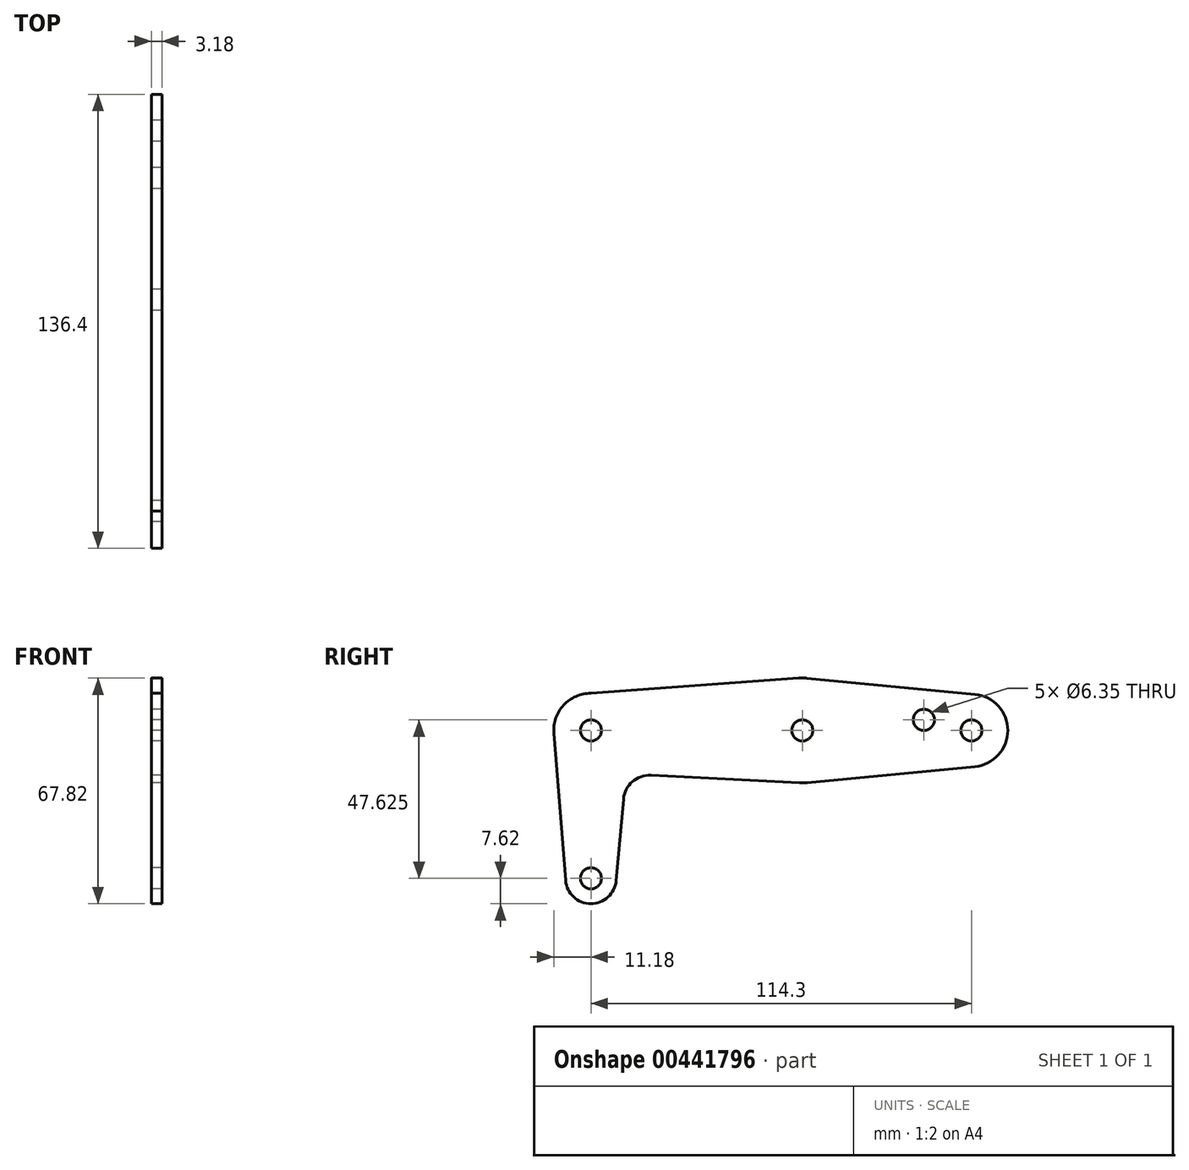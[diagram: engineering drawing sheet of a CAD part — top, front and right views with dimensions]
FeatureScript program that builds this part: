
annotation { "Feature Type Name" : "Feature", "Feature Type Description" : "" }
export const myFeature = defineFeature(function(context is Context, id is Id, definition is map)
    precondition{}
    {
        {
            var Q0;
            Q0=qCreatedBy(makeId("Right.planeOp"),FACE);
            var sketch = newSketch(context, id + "F0", { "sketchPlane" : qUnion([Q0])});
            skArc(sketch, "E0", {"start": v(1.5, 15.68) * mm, "mid": v(0.18, 15.75) * mm, "end": v(-1.13, 15.7) * mm});
            skLineSegment(sketch, "E1", {"start": v(0, 0) * mm, "end": v(-80.01, 0) * mm});
            skLineSegment(sketch, "E2", {"start": v(0, 0) * mm, "end": v(68.5, 0) * mm});
            skLineSegment(sketch, "E3.0", {"start": v(-54.4, -44.45) * mm, "end": v(-72.8, -44.45) * mm});
            skLineSegment(sketch, "E4", {"start": v(0, 22.2) * mm, "end": v(0, -18.9) * mm});
            skLineSegment(sketch, "E5.0", {"start": v(-63.5, 11.2) * mm, "end": v(-63.5, -52.07) * mm});
            skArc(sketch, "E6", {"start": v(-71.1, -45.06) * mm, "mid": v(-63.54, -52.07) * mm, "end": v(-55.91, -45.13) * mm});
            skArc(sketch, "E7", {"start": v(-63.5, 11.18) * mm, "mid": v(-71.71, 7.58) * mm, "end": v(-74.64, -0.9) * mm});
            skLineSegment(sketch, "E8", {"start": v(-74.64, -0.9) * mm, "end": v(-71.1, -45.06) * mm});
            skLineSegment(sketch, "E9.0", {"start": v(-45.87, -21.34) * mm, "end": v(-80.01, -21.34) * mm});
            skLineSegment(sketch, "E10.0", {"start": v(-45.87, 12.48) * mm, "end": v(-45.87, -21.34) * mm});
            skLineSegment(sketch, "E11.0", {"start": v(50.8, 3.18) * mm, "end": v(50.8, -3.18) * mm});
            skArc(sketch, "E12", {"start": v(51.84, -10.87) * mm, "mid": v(61.72, 0) * mm, "end": v(51.84, 10.87) * mm});
            skLineSegment(sketch, "E13", {"start": v(1.5, 15.68) * mm, "end": v(51.84, 10.87) * mm});
            skLineSegment(sketch, "E14", {"start": v(1.5, -15.68) * mm, "end": v(51.84, -10.87) * mm});
            skCircle(sketch, "E15", {"center": v(50.8, 0) * mm, "radius": 3.18 * mm});
            skCircle(sketch, "E16", {"center": v(0, 0) * mm, "radius": 3.18 * mm});
            skLineSegment(sketch, "E17", {"start": v(-1.13, 15.7) * mm, "end": v(-64.3, 11.15) * mm});
            skLineSegment(sketch, "E18", {"start": v(-53.71, -20.63) * mm, "end": v(-55.91, -45.13) * mm});
            skLineSegment(sketch, "E19", {"start": v(-0.8, -15.73) * mm, "end": v(-45.48, -13.47) * mm});
            skArc(sketch, "E20.filletArc", {"start": v(-45.48, -13.47) * mm, "mid": v(-51.04, -15.4) * mm, "end": v(-53.71, -20.63) * mm});
            skArc(sketch, "E21.trimOffspring", {"start": v(-0.8, -15.73) * mm, "mid": v(0.35, -15.74) * mm, "end": v(1.5, -15.68) * mm});
            skCircle(sketch, "E22", {"center": v(-63.5, 0) * mm, "radius": 3.18 * mm});
            skCircle(sketch, "E23", {"center": v(-63.5, -44.45) * mm, "radius": 3.18 * mm});
            skLineSegment(sketch, "E24.0", {"start": v(36.53, 6.35) * mm, "end": v(36.53, 0) * mm});
            skLineSegment(sketch, "E25.0", {"start": v(33.35, 3.18) * mm, "end": v(39.7, 3.18) * mm});
            skCircle(sketch, "E26", {"center": v(36.53, 3.18) * mm, "radius": 3.18 * mm});
            skSolve(sketch);
        }
        {
            var Q0;
            {var subQ6=sQuery(id+"F0.wireOp",EDGE,"E19");Q0=makeQuery(id+"F0.imprint","IMPRINT",FACE,{"disambiguationData":[TD([[makeQuery(id+"F0.imprint","IMPRINT",EDGE,{"derivedFrom":subQ6}),-1.0]])]});}
            var Q1;
            {var subQ14=sQuery(id+"F0.wireOp",EDGE,"E14");Q1=makeQuery(id+"F0.imprint","IMPRINT",FACE,{"disambiguationData":[TD([[makeQuery(id+"F0.imprint","IMPRINT",EDGE,{"derivedFrom":subQ14}),1.0]])]});}
            var Q2;
            {var subQ4=sQuery(id+"F0.wireOp",EDGE,"E13");Q2=makeQuery(id+"F0.imprint","IMPRINT",FACE,{"disambiguationData":[TD([[makeQuery(id+"F0.imprint","IMPRINT",EDGE,{"derivedFrom":subQ4}),-1.0]])]});}
            var Q3;
            {var subQ0=sQuery(id+"F0.wireOp",EDGE,"E17");var subQ6=sQuery(id+"F0.wireOp",EDGE,"E0");var subQ11=makeQuery(id+"F0.imprint","INTERSECT",VERTEX,{"derivedFrom":[subQ6,subQ0]});Q3=makeQuery(id+"F0.imprint","IMPRINT",FACE,{"disambiguationData":[TD([[makeQuery(id+"F0.imprint","IMPRINT",EDGE,{"disambiguationData":[TD([[subQ11,1.0]])],"derivedFrom":subQ6}),1.0]])]});}
            var Q4;
            {var subQ5=sQuery(id+"F0.wireOp",EDGE,"E10.0");var subQ7=sQuery(id+"F0.wireOp",EDGE,"E1");var subQ8=makeQuery(id+"F0.imprint","INTERSECT",VERTEX,{"derivedFrom":[subQ7,subQ5]});Q4=makeQuery(id+"F0.imprint","IMPRINT",FACE,{"disambiguationData":[TD([[makeQuery(id+"F0.imprint","IMPRINT",EDGE,{"disambiguationData":[TD([[subQ8,-1.0]])],"derivedFrom":subQ7}),-1.0]])]});}
            var Q5;
            {var subQ1=sQuery(id+"F0.wireOp",EDGE,"E10.0");var subQ3=sQuery(id+"F0.wireOp",EDGE,"E1");var subQ4=makeQuery(id+"F0.imprint","INTERSECT",VERTEX,{"derivedFrom":[subQ3,subQ1]});Q5=makeQuery(id+"F0.imprint","IMPRINT",FACE,{"disambiguationData":[TD([[makeQuery(id+"F0.imprint","IMPRINT",EDGE,{"disambiguationData":[TD([[subQ4,-1.0]])],"derivedFrom":subQ3}),1.0]])]});}
            var Q6;
            {var subQ1=sQuery(id+"F0.wireOp",EDGE,"E7");var subQ3=sQuery(id+"F0.wireOp",EDGE,"E1");var subQ4=makeQuery(id+"F0.imprint","INTERSECT",VERTEX,{"derivedFrom":[subQ3,subQ1]});Q6=makeQuery(id+"F0.imprint","IMPRINT",FACE,{"disambiguationData":[TD([[makeQuery(id+"F0.imprint","IMPRINT",EDGE,{"disambiguationData":[TD([[subQ4,1.0]])],"derivedFrom":subQ3}),1.0]])]});}
            var Q7;
            {var subQ0=sQuery(id+"F0.wireOp",EDGE,"E7");var subQ2=sQuery(id+"F0.wireOp",EDGE,"E1");var subQ3=makeQuery(id+"F0.imprint","INTERSECT",VERTEX,{"derivedFrom":[subQ2,subQ0]});Q7=makeQuery(id+"F0.imprint","IMPRINT",FACE,{"disambiguationData":[TD([[makeQuery(id+"F0.imprint","IMPRINT",EDGE,{"disambiguationData":[TD([[subQ3,1.0]])],"derivedFrom":subQ2}),-1.0]])]});}
            var Q8;
            {var subQ0=sQuery(id+"F0.wireOp",EDGE,"E18");var subQ1=sQuery(id+"F0.wireOp",EDGE,"E3.0");var subQ2=makeQuery(id+"F0.imprint","INTERSECT",VERTEX,{"derivedFrom":[subQ1,subQ0]});Q8=makeQuery(id+"F0.imprint","IMPRINT",FACE,{"disambiguationData":[TD([[makeQuery(id+"F0.imprint","IMPRINT",EDGE,{"disambiguationData":[TD([[subQ2,-1.0]])],"derivedFrom":subQ1}),-1.0]])]});}
            var Q9;
            {var subQ1=sQuery(id+"F0.wireOp",EDGE,"E8");var subQ5=sQuery(id+"F0.wireOp",EDGE,"E3.0");var subQ6=makeQuery(id+"F0.imprint","INTERSECT",VERTEX,{"derivedFrom":[subQ5,subQ1]});Q9=makeQuery(id+"F0.imprint","IMPRINT",FACE,{"disambiguationData":[TD([[makeQuery(id+"F0.imprint","IMPRINT",EDGE,{"disambiguationData":[TD([[subQ6,1.0]])],"derivedFrom":subQ5}),-1.0]])]});}
            var Q10;
            {var subQ3=sQuery(id+"F0.wireOp",EDGE,"E18");var subQ7=sQuery(id+"F0.wireOp",EDGE,"E3.0");var subQ8=makeQuery(id+"F0.imprint","INTERSECT",VERTEX,{"derivedFrom":[subQ7,subQ3]});Q10=makeQuery(id+"F0.imprint","IMPRINT",FACE,{"disambiguationData":[TD([[makeQuery(id+"F0.imprint","IMPRINT",EDGE,{"disambiguationData":[TD([[subQ8,-1.0]])],"derivedFrom":subQ7}),1.0]])]});}
            var Q11;
            {var subQ0=sQuery(id+"F0.wireOp",EDGE,"E8");var subQ3=sQuery(id+"F0.wireOp",EDGE,"E3.0");var subQ4=makeQuery(id+"F0.imprint","INTERSECT",VERTEX,{"derivedFrom":[subQ3,subQ0]});Q11=makeQuery(id+"F0.imprint","IMPRINT",FACE,{"disambiguationData":[TD([[makeQuery(id+"F0.imprint","IMPRINT",EDGE,{"disambiguationData":[TD([[subQ4,1.0]])],"derivedFrom":subQ3}),1.0]])]});}
            extrude(context, id + "F1", {"entities" : qUnion([Q0, Q1, Q2, Q3, Q4, Q5, Q6, Q7, Q8, Q9, Q10, Q11]), "endBound" : BoundingType.SYMMETRIC, "depth" : 3.17 * mm});
        }
    });
